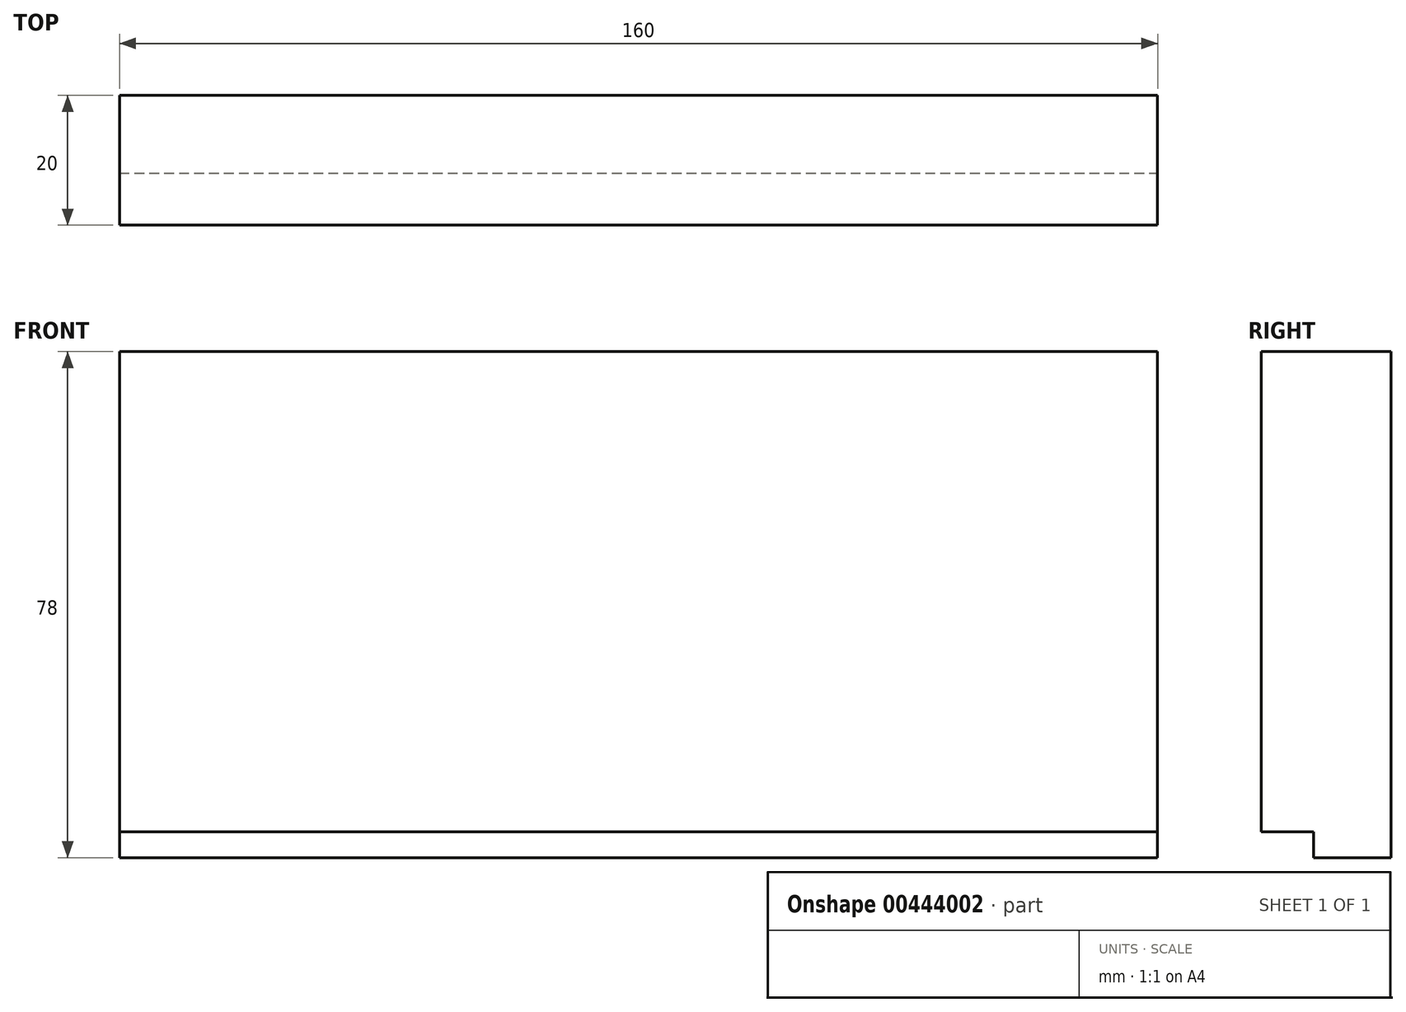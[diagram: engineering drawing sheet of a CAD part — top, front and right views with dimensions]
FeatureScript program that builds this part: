
annotation { "Feature Type Name" : "Feature", "Feature Type Description" : "" }
export const myFeature = defineFeature(function(context is Context, id is Id, definition is map)
    precondition{}
    {
        {
            var Q0;
            Q0=qCreatedBy(makeId("Front.planeOp"),FACE);
            var sketch = newSketch(context, id + "F0", { "sketchPlane" : qUnion([Q0])});
            skLineSegment(sketch, "E0.bottom", {"start": v(-68.76, 51.22) * mm, "end": v(91.24, 51.22) * mm});
            skLineSegment(sketch, "E0.top", {"start": v(-68.76, -26.78) * mm, "end": v(91.24, -26.78) * mm});
            skLineSegment(sketch, "E0.left", {"start": v(-68.76, 51.22) * mm, "end": v(-68.76, -26.78) * mm});
            skLineSegment(sketch, "E0.right", {"start": v(91.24, 51.22) * mm, "end": v(91.24, -26.78) * mm});
            skLineSegment(sketch, "E1", {"start": v(-68.76, -22.78) * mm, "end": v(91.24, -22.78) * mm});
            skSolve(sketch);
        }
        {
            var Q0;
            {var subQ0=sQuery(id+"F0.wireOp",EDGE,"E0.bottom");Q0=makeQuery(id+"F0.imprint","IMPRINT",FACE,{"disambiguationData":[TD([[makeQuery(id+"F0.imprint","IMPRINT",EDGE,{"derivedFrom":subQ0}),-1.0]])]});}
            extrude(context, id + "F1", {"entities" : qUnion([Q0]), "depth" : 20 * mm});
        }
        {
            var Q0;
            {var subQ0=sQuery(id+"F0.wireOp",EDGE,"E0.top");Q0=makeQuery(id+"F0.imprint","IMPRINT",FACE,{"disambiguationData":[TD([[makeQuery(id+"F0.imprint","IMPRINT",EDGE,{"derivedFrom":subQ0}),1.0]])]});}
            extrude(context, id + "F2", {"entities" : qUnion([Q0]), "operationType" : NewBodyOperationType.ADD, "depth" : 12 * mm});
        }
    });
